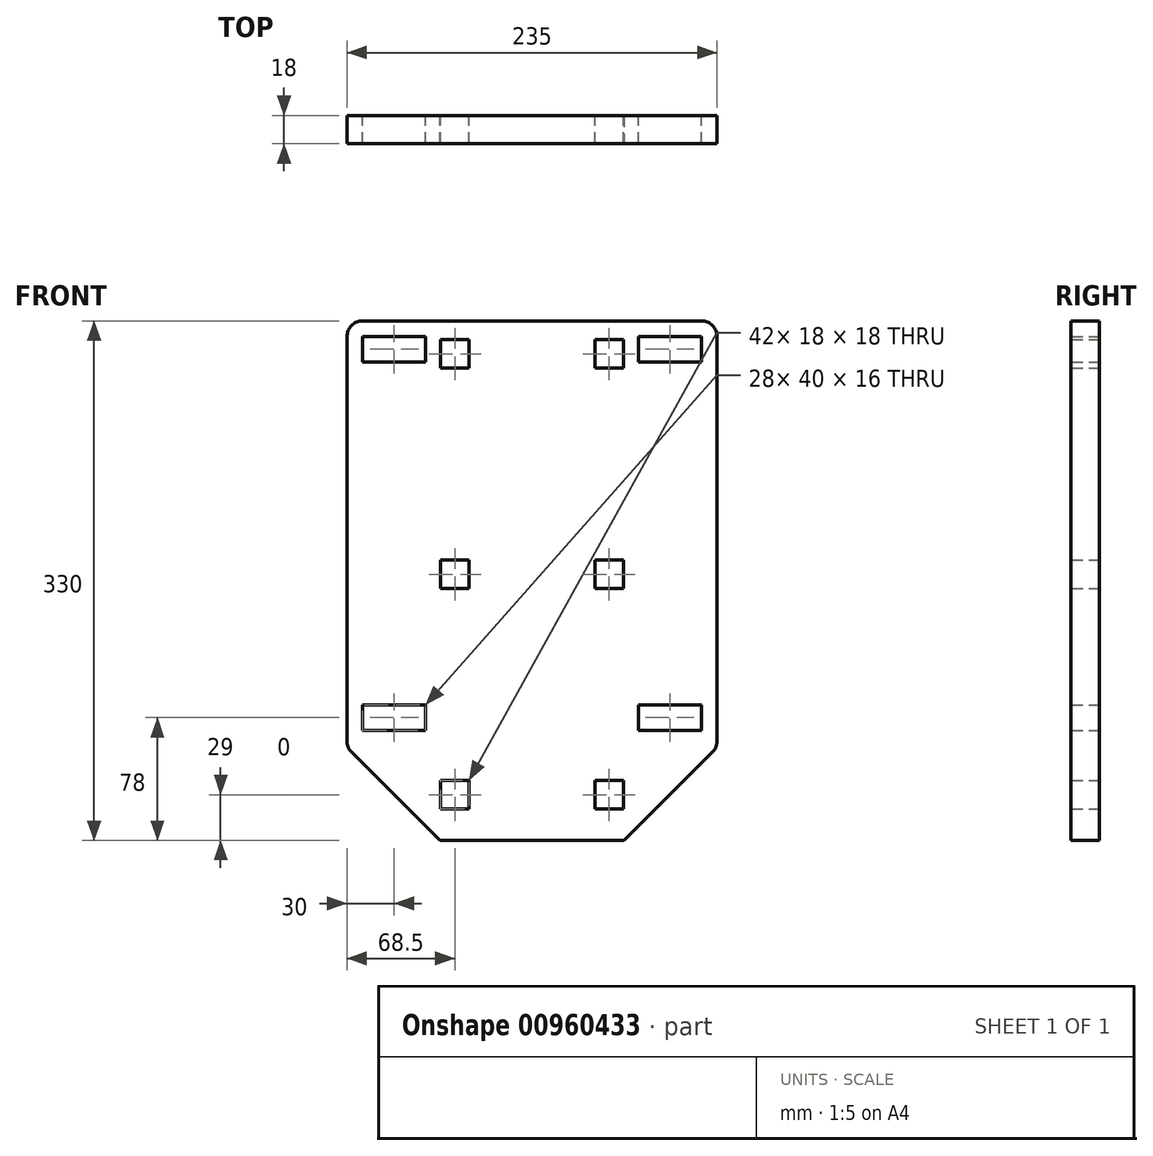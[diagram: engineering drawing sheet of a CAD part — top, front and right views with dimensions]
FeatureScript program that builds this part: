
annotation { "Feature Type Name" : "Feature", "Feature Type Description" : "" }
export const myFeature = defineFeature(function(context is Context, id is Id, definition is map)
    precondition{}
    {
        {
            var Q0;
            Q0=qCreatedBy(makeId("Front.planeOp"),FACE);
            var sketch = newSketch(context, id + "F0", { "sketchPlane" : qUnion([Q0])});
            skLineSegment(sketch, "E0.bottom", {"start": v(117.5, 165) * mm, "end": v(-117.5, 165) * mm});
            skLineSegment(sketch, "E0.top", {"start": v(117.5, -165) * mm, "end": v(-117.5, -165) * mm});
            skLineSegment(sketch, "E0.left", {"start": v(117.5, 165) * mm, "end": v(117.5, -165) * mm});
            skLineSegment(sketch, "E0.right", {"start": v(-117.5, 165) * mm, "end": v(-117.5, -165) * mm});
            skPoint(sketch, "E0.middle", {"position": v(0, 0) * mm});
            skLineSegment(sketch, "E1.bottom", {"start": v(67.5, 155) * mm, "end": v(107.5, 155) * mm});
            skLineSegment(sketch, "E1.top", {"start": v(67.5, 139) * mm, "end": v(107.5, 139) * mm});
            skLineSegment(sketch, "E1.left", {"start": v(67.5, 155) * mm, "end": v(67.5, 139) * mm});
            skLineSegment(sketch, "E1.right", {"start": v(107.5, 155) * mm, "end": v(107.5, 139) * mm});
            skPoint(sketch, "E1.middle", {"position": v(87.5, 147) * mm});
            skLineSegment(sketch, "E2", {"start": v(0, 203.48) * mm, "end": v(0, -201.03) * mm, "construction": true});
            skPoint(sketch, "E2.endSnap0", {"position": v(0, -165) * mm});
            skLineSegment(sketch, "E3", {"start": v(-157.99, 0) * mm, "end": v(149.05, 0) * mm, "construction": true});
            skLineSegment(sketch, "E4.MirrorCS", {"start": v(-67.5, 139) * mm, "end": v(-107.5, 139) * mm});
            skLineSegment(sketch, "E5.MirrorCS", {"start": v(-67.5, 155) * mm, "end": v(-67.5, 139) * mm});
            skLineSegment(sketch, "E6.MirrorCS", {"start": v(-67.5, 155) * mm, "end": v(-107.5, 155) * mm});
            skLineSegment(sketch, "E7.MirrorCS", {"start": v(-107.5, 155) * mm, "end": v(-107.5, 139) * mm});
            skLineSegment(sketch, "E8", {"start": v(-124.42, 30) * mm, "end": v(148.57, 30) * mm, "construction": true});
            skLineSegment(sketch, "E9.MirrorCS", {"start": v(-67.5, -95) * mm, "end": v(-67.5, -79) * mm});
            skLineSegment(sketch, "E10.MirrorCS", {"start": v(-67.5, -95) * mm, "end": v(-107.5, -95) * mm});
            skLineSegment(sketch, "E11.MirrorCS", {"start": v(-67.5, -79) * mm, "end": v(-107.5, -79) * mm});
            skLineSegment(sketch, "E12.MirrorCS", {"start": v(-107.5, -95) * mm, "end": v(-107.5, -79) * mm});
            skLineSegment(sketch, "E13.MirrorCS", {"start": v(107.5, -95) * mm, "end": v(107.5, -79) * mm});
            skLineSegment(sketch, "E14.MirrorCS", {"start": v(67.5, -95) * mm, "end": v(107.5, -95) * mm});
            skLineSegment(sketch, "E15.MirrorCS", {"start": v(67.5, -95) * mm, "end": v(67.5, -79) * mm});
            skLineSegment(sketch, "E16.MirrorCS", {"start": v(67.5, -79) * mm, "end": v(107.5, -79) * mm});
            skLineSegment(sketch, "E17.bottom", {"start": v(58, -145) * mm, "end": v(40, -145) * mm});
            skLineSegment(sketch, "E17.top", {"start": v(58, -127) * mm, "end": v(40, -127) * mm});
            skLineSegment(sketch, "E17.left", {"start": v(58, -145) * mm, "end": v(58, -127) * mm});
            skLineSegment(sketch, "E17.right", {"start": v(40, -145) * mm, "end": v(40, -127) * mm});
            skPoint(sketch, "E17.middle", {"position": v(49, -136) * mm});
            skLineSegment(sketch, "E18.MirrorCS", {"start": v(-40, -145) * mm, "end": v(-40, -127) * mm});
            skLineSegment(sketch, "E19.MirrorCS", {"start": v(-58, -145) * mm, "end": v(-40, -145) * mm});
            skLineSegment(sketch, "E20.MirrorCS", {"start": v(-58, -145) * mm, "end": v(-58, -127) * mm});
            skLineSegment(sketch, "E21.MirrorCS", {"start": v(-58, -127) * mm, "end": v(-40, -127) * mm});
            skLineSegment(sketch, "E22.0.1.0", {"start": v(-58, 13) * mm, "end": v(-40, 13) * mm});
            skLineSegment(sketch, "E22.0.1.1", {"start": v(-58, -5) * mm, "end": v(-58, 13) * mm});
            skLineSegment(sketch, "E22.0.1.2", {"start": v(-58, -5) * mm, "end": v(-40, -5) * mm});
            skLineSegment(sketch, "E22.0.1.3", {"start": v(-40, -5) * mm, "end": v(-40, 13) * mm});
            skLineSegment(sketch, "E22.0.1.4", {"start": v(40, -5) * mm, "end": v(40, 13) * mm});
            skLineSegment(sketch, "E22.0.1.5", {"start": v(58, -5) * mm, "end": v(58, 13) * mm});
            skLineSegment(sketch, "E22.0.1.6", {"start": v(58, 13) * mm, "end": v(40, 13) * mm});
            skLineSegment(sketch, "E22.0.1.7", {"start": v(58, -5) * mm, "end": v(40, -5) * mm});
            skLineSegment(sketch, "E22.0.2.0", {"start": v(-58, 153) * mm, "end": v(-40, 153) * mm});
            skLineSegment(sketch, "E22.0.2.1", {"start": v(-58, 135) * mm, "end": v(-58, 153) * mm});
            skLineSegment(sketch, "E22.0.2.2", {"start": v(-58, 135) * mm, "end": v(-40, 135) * mm});
            skLineSegment(sketch, "E22.0.2.3", {"start": v(-40, 135) * mm, "end": v(-40, 153) * mm});
            skLineSegment(sketch, "E22.0.2.4", {"start": v(40, 135) * mm, "end": v(40, 153) * mm});
            skLineSegment(sketch, "E22.0.2.5", {"start": v(58, 135) * mm, "end": v(58, 153) * mm});
            skLineSegment(sketch, "E22.0.2.6", {"start": v(58, 153) * mm, "end": v(40, 153) * mm});
            skLineSegment(sketch, "E22.0.2.7", {"start": v(58, 135) * mm, "end": v(40, 135) * mm});
            skLineSegment(sketch, "E22.direction1", {"start": v(-58, -127) * mm, "end": v(-33, -127) * mm, "construction": true});
            skLineSegment(sketch, "E22.direction2", {"start": v(-58, -127) * mm, "end": v(-58, 13) * mm, "construction": true});
            skSolve(sketch);
        }
        {
            var Q0;
            Q0 = qSketchRegion(id + "F0", true);
            extrude(context, id + "F1", {"entities" : qUnion([Q0]), "depth" : 18 * mm, "offsetDistance" : 25 * mm});
        }
        {
            var Q0;
            Q0=makeQuery(id+"F1.opExtrude","SWEPT_EDGE",EDGE,{"disambiguationData":[OSD([sQuery(id+"F0.wireOp",EDGE,"E0.top"),sQuery(id+"F0.wireOp",EDGE,"E0.left")])]});
            var Q1;
            Q1=makeQuery(id+"F1.opExtrude","SWEPT_EDGE",EDGE,{"disambiguationData":[OSD([sQuery(id+"F0.wireOp",EDGE,"E0.top"),sQuery(id+"F0.wireOp",EDGE,"E0.right")])]});
            chamfer(context, id + "F2", {"entities" : qUnion([Q0, Q1]), "width" : 59 * mm, "tangentPropagation" : true});
        }
        {
            var Q0;
            Q0=makeQuery(id+"F1.opExtrude","SWEPT_EDGE",EDGE,{"disambiguationData":[OSD([sQuery(id+"F0.wireOp",EDGE,"E0.bottom"),sQuery(id+"F0.wireOp",EDGE,"E0.left")])]});
            var Q1;
            {var subQ0=sQuery(id+"F0.wireOp",EDGE,"E0.left");Q1=makeQuery(id+"F2.opChamfer","BLEND_EDGE",EDGE,{"blendedFrom":[makeQuery(id+"F1.opExtrude","SWEPT_EDGE",EDGE,{"disambiguationData":[OSD([sQuery(id+"F0.wireOp",EDGE,"E0.top"),subQ0])]}),makeQuery(id+"F1.opExtrude","SWEPT_FACE",FACE,{"disambiguationData":[OSD([subQ0])]})],"blendedInto":[makeQuery(id+"F1.opExtrude","SWEPT_FACE",FACE,{"disambiguationData":[OSD([subQ0])]})]});}
            var Q2;
            Q2=makeQuery(id+"F1.opExtrude","SWEPT_EDGE",EDGE,{"disambiguationData":[OSD([sQuery(id+"F0.wireOp",EDGE,"E0.bottom"),sQuery(id+"F0.wireOp",EDGE,"E0.right")])]});
            var Q3;
            {var subQ0=sQuery(id+"F0.wireOp",EDGE,"E0.right");Q3=makeQuery(id+"F2.opChamfer","BLEND_EDGE",EDGE,{"blendedFrom":[makeQuery(id+"F1.opExtrude","SWEPT_EDGE",EDGE,{"disambiguationData":[OSD([sQuery(id+"F0.wireOp",EDGE,"E0.top"),subQ0])]}),makeQuery(id+"F1.opExtrude","SWEPT_FACE",FACE,{"disambiguationData":[OSD([subQ0])]})],"blendedInto":[makeQuery(id+"F1.opExtrude","SWEPT_FACE",FACE,{"disambiguationData":[OSD([subQ0])]})]});}
            fillet(context, id + "F3", {"entities" : qUnion([Q0, Q1, Q2, Q3]), "radius" : 10 * mm, "tangentPropagation" : true, "allowEdgeOverflow" : false});
        }
    });
